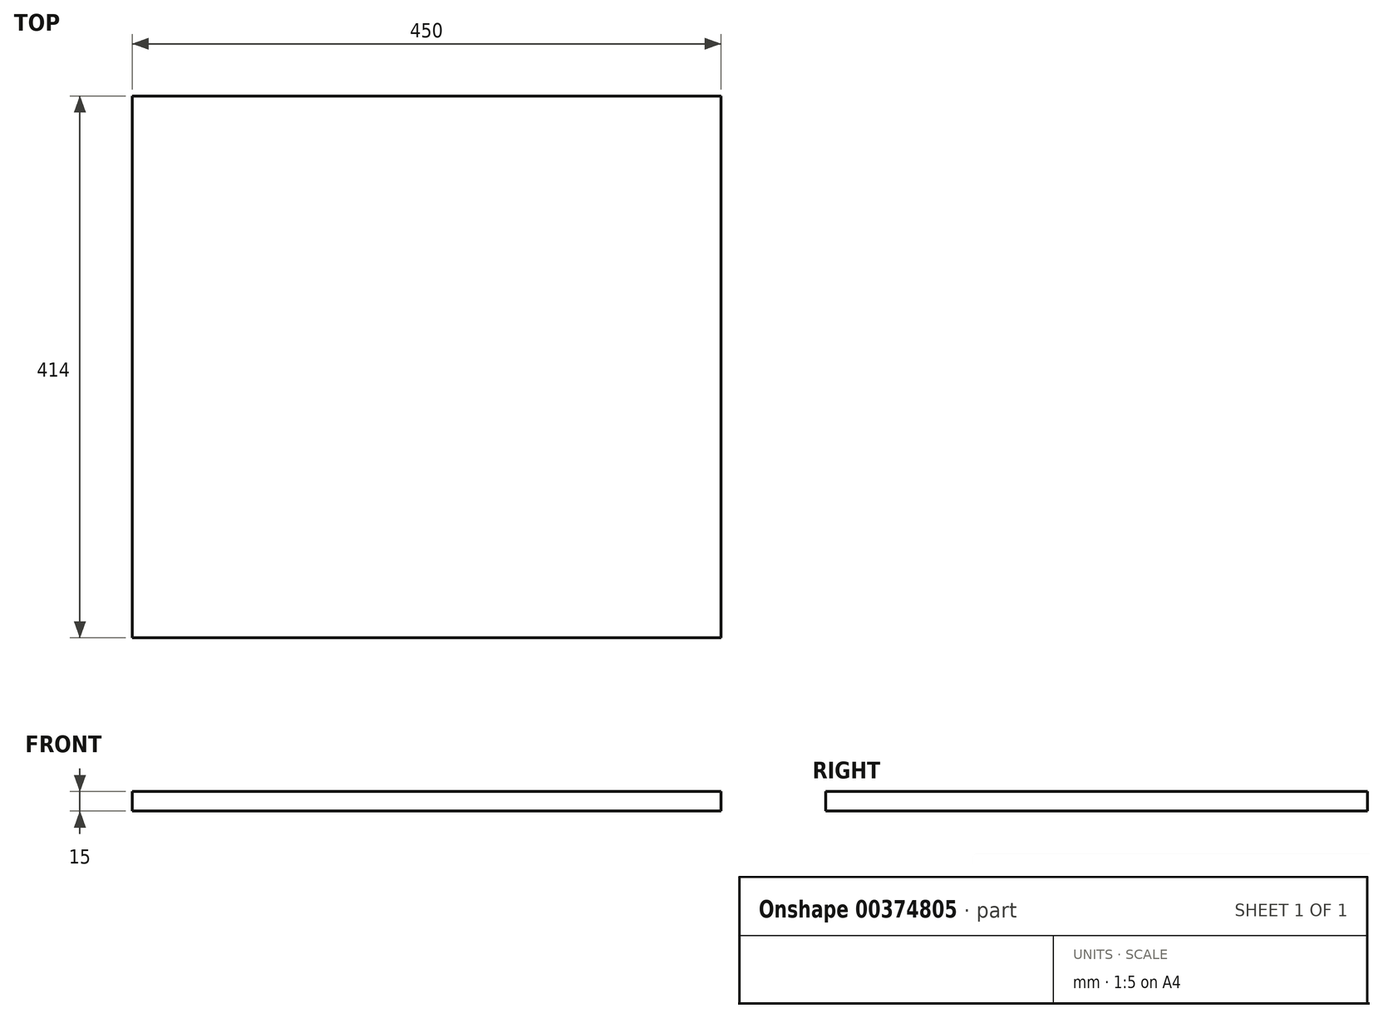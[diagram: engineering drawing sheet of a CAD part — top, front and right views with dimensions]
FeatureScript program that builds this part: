
annotation { "Feature Type Name" : "Feature", "Feature Type Description" : "" }
export const myFeature = defineFeature(function(context is Context, id is Id, definition is map)
    precondition{}
    {
        {
            var Q0;
            Q0=qCreatedBy(makeId("Top.planeOp"),FACE);
            var sketch = newSketch(context, id + "F0", { "sketchPlane" : qUnion([Q0])});
            skLineSegment(sketch, "E0.bottom", {"start": v(225, -207) * mm, "end": v(-225, -207) * mm});
            skLineSegment(sketch, "E0.top", {"start": v(225, 207) * mm, "end": v(-225, 207) * mm});
            skLineSegment(sketch, "E0.left", {"start": v(225, -207) * mm, "end": v(225, 207) * mm});
            skLineSegment(sketch, "E0.right", {"start": v(-225, -207) * mm, "end": v(-225, 207) * mm});
            skPoint(sketch, "E0.middle", {"position": v(0, 0) * mm});
            skSolve(sketch);
        }
        {
            var Q0;
            Q0=makeQuery(id+"F0.imprint","IMPRINT",FACE,{"disambiguationData":[TD([[makeQuery(id+"F0.imprint","IMPRINT",EDGE,{"derivedFrom":sQuery(id+"F0.wireOp",EDGE,"E0.bottom")}),-1.0]])]});
            extrude(context, id + "F1", {"entities" : qUnion([Q0]), "depth" : 15 * mm});
        }
    });
